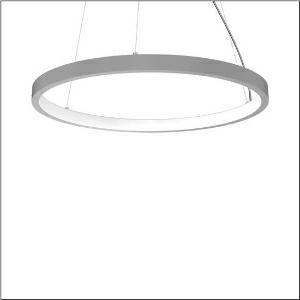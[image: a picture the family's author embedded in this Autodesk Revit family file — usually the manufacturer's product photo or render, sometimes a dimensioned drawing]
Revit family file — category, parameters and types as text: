
# Revit family: silica_r__21_ring-i_5pjbi4d3204a_cd14
name_source: partatom
category: Lighting Fixtures
units: mm (PartAtom-declared; Revit-internal decimal feet)

## family parameters
Cut with Voids When Loaded = No
Host = Face
Light Source = No
Part Type = Normal
Room Calculation Point = No
Round Connector Dimension = Use Diameter
Shared = No

## types (1)
- Silica® 21 Ring-I (1 x LED, 8890 lm, 140 W, 4000K)
    Apparent Load = 140 VA
    CIE Flux Codes = 22 48 76 50 101
    Color Rendering = 80
    Color Temperature = 4000K
    Default Elevation = 1800 mm
    Description = Silica® 21 Ring-I, suspended luminaire, of PMMA, frosted, light emission: inner ring side luminous distribution, primary light characteristic: symmetric, installation type: suspended mounting, LED, rated luminous flux: 8.890lm, luminous efficacy: 64lm/W, light colour: 840, colour temperature: 4000K, control gear: DALI 2, with terminal, 5-pole, mains connection: 230V, AC/DC, 0/50..60Hz, rated input power: 140W, housing, of extruded aluminium section, metallic grey (RAL 9006), diameter: 1.470mm, ceiling canopy, metallic grey (RAL 9006), protection rating (lamp compartment): IP40, insulation class (complete): insulation class I (protective earthing), certification: CE, impact resistance: IK02, permissible operating ambient temperature: 0..+35°C, packaging unit: 1 piece
    Height = 48 mm  [stored 0.15748 ft]
    Lamp = 1 x LED
    Lamp Light Flux = 8890 lm
    Lamp Power = 140 W
    Lamp count = 1
    Length = 1470 mm
    Luminous efficacy = 64 lm/W
    Manufacturer = Siteco
    ModVariant = No
    Model = 5PJBI4D3204A
    Mounting Place = Ceiling
    Mounting Type = Pendant
    Number of Poles = 1
    OnlyDefault = Yes
    Power Factor = 1
    Product Name = Silica® 21 Ring-I
    Product group = suspended luminaire
    ProductGroupID = 905
    Protection Class = Protection class I
    Protection Degree = IP 40
    RLX_Detail_Level = 1
    RLX_Emergency_Light_Flux = 0 lm
    RLX_Emergency_Type = 0
    RLX_Emergency_Type_DB = No
    RlxData = <blob elided: 18853 chars, md5=9cf8fb96>
    Socket = socket
    Standby Power = 0 W
    System Light Flux = 8890 lm
    System Power = 140 W
    Type Comments = Product without accessories
    Type Image = l_1251756.jpg
    URL = http://relux.com
    VarID = ---
    Voltage = 0 V
    Weight = 0.00 kg
    Width = 0 mm  [stored 0 ft]

note: [stored X ft] marks values corroborated as IEEE doubles in the binary element streams (Revit-internal decimal feet)

## geometry (parser evidence)
native form markers: Blend x4, Sweep x13
no freeform markers — native parametric forms only
